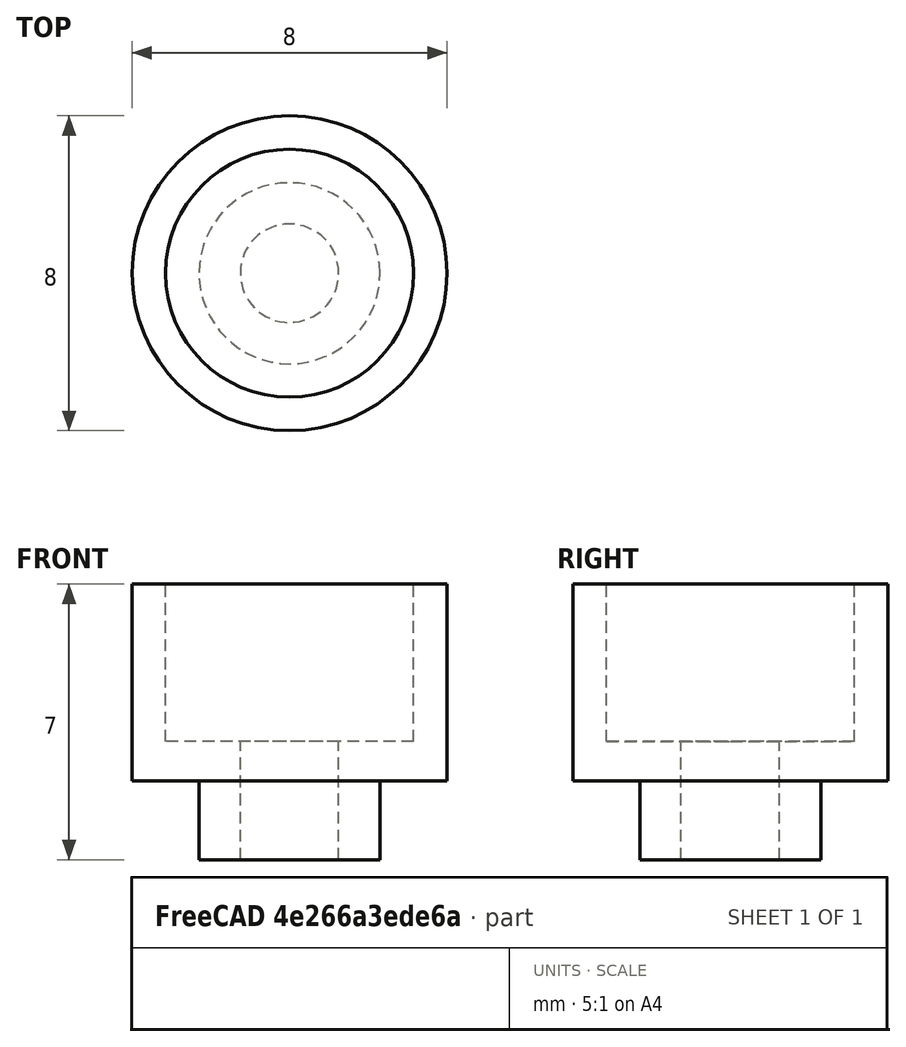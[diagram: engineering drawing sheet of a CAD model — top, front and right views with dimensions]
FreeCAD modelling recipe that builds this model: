
FCSTD DOCUMENT  (FreeCAD 0.18R14555 (Git shallow))
Label: extruder-magnet-mounter
License: All rights reserved
LicenseURL: http://en.wikipedia.org/wiki/All_rights_reserved
objects: Part::Cylinder×4, Part::MultiFuse×2, Part::Feature×2
note: 8 computed .brp shape members not serialized (recipe doc carries the construction recipe); baked Part::Feature solids carry a one-line shape summary decoded from their .brp

FEATURE [Part::Cylinder] Cylinder004
  Angle = 360
  AttacherType = Attacher::AttachEngine3D
  Height = 2
  Radius = 2.3
FEATURE [Part::Cylinder] Cylinder005
  Angle = 360
  AttacherType = Attacher::AttachEngine3D
  Height = 4
  Radius = 1.25
  expr: Radius = 2.5 / 2
FEATURE [Part::Cylinder] Cylinder
  Angle = 360
  AttacherType = Attacher::AttachEngine3D
  Height = 4
  Placement = pos=(0,0,3) rot=(0,0,1;0rad)
  Radius = 3.15
FEATURE [Part::Cylinder] Cylinder006
  Angle = 360
  AttacherType = Attacher::AttachEngine3D
  Height = 5
  Placement = pos=(0,0,2) rot=(0,0,1;0rad)
  Radius = 4
FEATURE [Part::MultiFuse] Fusion
  Shapes = -> [Cylinder006,Cylinder004]
FEATURE [Part::MultiFuse] Fusion001
  Shapes = -> [Cylinder,Cylinder005]
FEATURE [Part::Feature] Fusion001001  label="Fusion002"
  shape: bbox 6.3 x 6.3 x 7 mm, 5 faces (baked)
FEATURE [Part::Feature] Fusion001002  label="Fusion003"
  shape: bbox 8 x 8 x 7 mm, 5 faces (baked)
